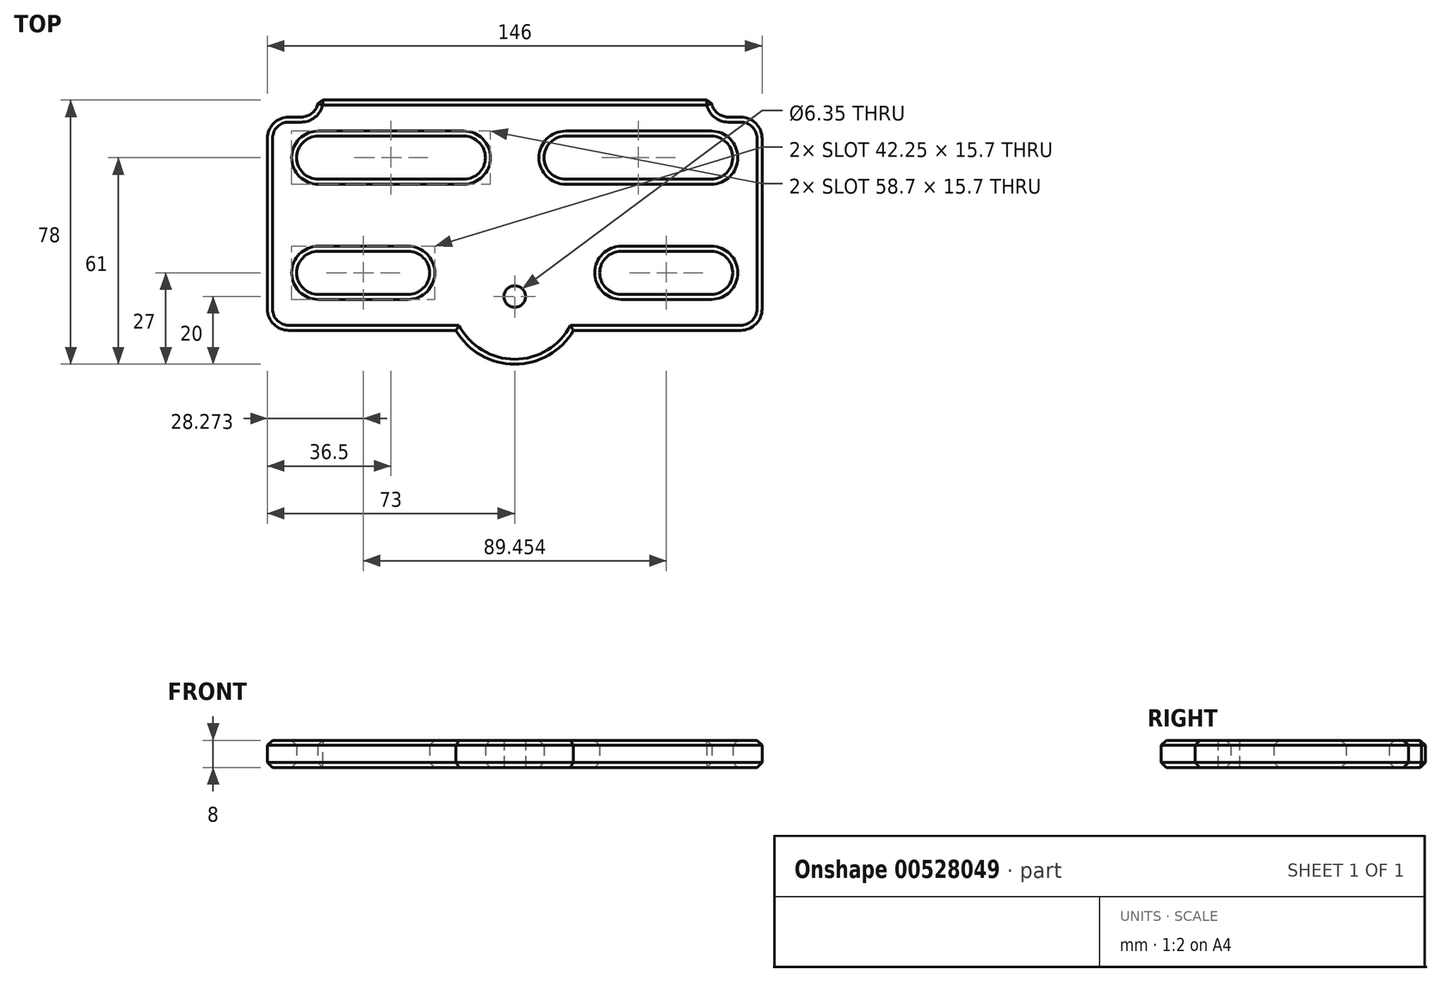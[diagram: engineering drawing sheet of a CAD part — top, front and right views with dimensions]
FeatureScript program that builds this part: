
annotation { "Feature Type Name" : "Feature", "Feature Type Description" : "" }
export const myFeature = defineFeature(function(context is Context, id is Id, definition is map)
    precondition{}
    {
        {
            var Q0;
            Q0=qCreatedBy(makeId("Top.planeOp"),FACE);
            var sketch = newSketch(context, id + "F0", { "sketchPlane" : qUnion([Q0])});
            skLineSegment(sketch, "E0", {"start": v(-66.65, -34) * mm, "end": v(-17.32, -34) * mm});
            skLineSegment(sketch, "E1", {"start": v(73, -27.65) * mm, "end": v(73, 22.65) * mm});
            skLineSegment(sketch, "E2", {"start": v(58, 34) * mm, "end": v(-58, 34) * mm});
            skLineSegment(sketch, "E3", {"start": v(-73, 22.65) * mm, "end": v(-73, -27.65) * mm});
            skArc(sketch, "E4", {"start": v(-17.32, -34) * mm, "mid": v(0, -44) * mm, "end": v(17.32, -34) * mm});
            skLineSegment(sketch, "E5.top", {"start": v(-66.65, 29) * mm, "end": v(-63, 29) * mm});
            skLineSegment(sketch, "E5.right", {"start": v(-58, 34) * mm, "end": v(-58, 34) * mm});
            skPoint(sketch, "E6.visualSharp", {"position": v(-58, 29) * mm});
            skArc(sketch, "E6.filletArc", {"start": v(-63, 29) * mm, "mid": v(-59.46, 30.46) * mm, "end": v(-58, 34) * mm});
            skLineSegment(sketch, "E7.top", {"start": v(66.65, 29) * mm, "end": v(63, 29) * mm});
            skLineSegment(sketch, "E7.right", {"start": v(58, 34) * mm, "end": v(58, 34) * mm});
            skPoint(sketch, "E8.visualSharp", {"position": v(58, 29) * mm});
            skArc(sketch, "E8.filletArc", {"start": v(58, 34) * mm, "mid": v(59.46, 30.46) * mm, "end": v(63, 29) * mm});
            skLineSegment(sketch, "E9.trimOffspring", {"start": v(17.32, -34) * mm, "end": v(66.65, -34) * mm});
            skPoint(sketch, "E10.visualSharp", {"position": v(-73, 29) * mm});
            skArc(sketch, "E10.filletArc", {"start": v(-66.65, 29) * mm, "mid": v(-71.14, 27.14) * mm, "end": v(-73, 22.65) * mm});
            skPoint(sketch, "E11.visualSharp", {"position": v(-73, -34) * mm});
            skArc(sketch, "E11.filletArc", {"start": v(-73, -27.65) * mm, "mid": v(-71.14, -32.14) * mm, "end": v(-66.65, -34) * mm});
            skPoint(sketch, "E12.visualSharp", {"position": v(73, -34) * mm});
            skArc(sketch, "E12.filletArc", {"start": v(66.65, -34) * mm, "mid": v(71.14, -32.14) * mm, "end": v(73, -27.65) * mm});
            skPoint(sketch, "E13.visualSharp", {"position": v(73, 29) * mm});
            skArc(sketch, "E13.filletArc", {"start": v(73, 22.65) * mm, "mid": v(71.14, 27.14) * mm, "end": v(66.65, 29) * mm});
            skLineSegment(sketch, "E14", {"start": v(-58, 17) * mm, "end": v(-15, 17) * mm});
            skLineSegment(sketch, "E15.MirrorCS", {"start": v(58, 17) * mm, "end": v(15, 17) * mm});
            skArc(sketch, "E16.0.startCap", {"start": v(-58, 10.65) * mm, "mid": v(-64.35, 17) * mm, "end": v(-58, 23.35) * mm});
            skArc(sketch, "E16.0.endCap", {"start": v(-15, 23.35) * mm, "mid": v(-8.65, 17) * mm, "end": v(-15, 10.65) * mm});
            skLineSegment(sketch, "E16.0.left", {"start": v(-58, 23.35) * mm, "end": v(-15, 23.35) * mm});
            skLineSegment(sketch, "E16.0.right", {"start": v(-58, 10.65) * mm, "end": v(-15, 10.65) * mm});
            skArc(sketch, "E17.0.startCap", {"start": v(58, 23.35) * mm, "mid": v(64.35, 17) * mm, "end": v(58, 10.65) * mm});
            skArc(sketch, "E17.0.endCap", {"start": v(15, 10.65) * mm, "mid": v(8.65, 17) * mm, "end": v(15, 23.35) * mm});
            skLineSegment(sketch, "E17.0.left", {"start": v(58, 10.65) * mm, "end": v(15, 10.65) * mm});
            skLineSegment(sketch, "E17.0.right", {"start": v(58, 23.35) * mm, "end": v(15, 23.35) * mm});
            skLineSegment(sketch, "E18", {"start": v(31.45, -17) * mm, "end": v(58, -17) * mm});
            skLineSegment(sketch, "E19.MirrorCS", {"start": v(-31.45, -17) * mm, "end": v(-58, -17) * mm});
            skArc(sketch, "E20.0.startCap", {"start": v(31.45, -23.35) * mm, "mid": v(25.1, -17) * mm, "end": v(31.45, -10.65) * mm});
            skArc(sketch, "E20.0.endCap", {"start": v(58, -10.65) * mm, "mid": v(64.35, -17) * mm, "end": v(58, -23.35) * mm});
            skLineSegment(sketch, "E20.0.left", {"start": v(31.45, -10.65) * mm, "end": v(58, -10.65) * mm});
            skLineSegment(sketch, "E20.0.right", {"start": v(31.45, -23.35) * mm, "end": v(58, -23.35) * mm});
            skArc(sketch, "E21.0.startCap", {"start": v(-31.45, -10.65) * mm, "mid": v(-25.1, -17) * mm, "end": v(-31.45, -23.35) * mm});
            skArc(sketch, "E21.0.endCap", {"start": v(-58, -23.35) * mm, "mid": v(-64.35, -17) * mm, "end": v(-58, -10.65) * mm});
            skLineSegment(sketch, "E21.0.left", {"start": v(-31.45, -23.35) * mm, "end": v(-58, -23.35) * mm});
            skLineSegment(sketch, "E21.0.right", {"start": v(-31.45, -10.65) * mm, "end": v(-58, -10.65) * mm});
            skCircle(sketch, "E22", {"center": v(0, -24) * mm, "radius": 3.18 * mm});
            skSolve(sketch);
        }
        {
            var Q0;
            Q0=makeQuery(id+"F0.imprint","IMPRINT",FACE,{"disambiguationData":[TD([[makeQuery(id+"F0.imprint","IMPRINT",EDGE,{"derivedFrom":sQuery(id+"F0.wireOp",EDGE,"E0")}),1.0]])]});
            extrude(context, id + "F1", {"entities" : qUnion([Q0]), "depth" : 8 * mm, "offsetDistance" : 25.4 * mm});
        }
        {
            var Q0;
            Q0=makeQuery(id+"F1.opExtrude","CAP_EDGE",EDGE,{"disambiguationData":[OSD([sQuery(id+"F0.wireOp",EDGE,"E2")])],"isStart":false});
            var Q1;
            Q1=makeQuery(id+"F1.opExtrude","CAP_EDGE",EDGE,{"disambiguationData":[OSD([sQuery(id+"F0.wireOp",EDGE,"E9.trimOffspring")])],"isStart":false});
            var Q2;
            Q2=makeQuery(id+"F1.opExtrude","CAP_EDGE",EDGE,{"disambiguationData":[OSD([sQuery(id+"F0.wireOp",EDGE,"E0")])],"isStart":false});
            var Q3;
            Q3=makeQuery(id+"F1.opExtrude","CAP_EDGE",EDGE,{"disambiguationData":[OSD([sQuery(id+"F0.wireOp",EDGE,"E4")])],"isStart":false});
            var Q4;
            Q4=makeQuery(id+"F1.opExtrude","CAP_EDGE",EDGE,{"disambiguationData":[OSD([sQuery(id+"F0.wireOp",EDGE,"E21.0.left")])],"isStart":false});
            var Q5;
            Q5=makeQuery(id+"F1.opExtrude","CAP_EDGE",EDGE,{"disambiguationData":[OSD([sQuery(id+"F0.wireOp",EDGE,"E16.0.right")])],"isStart":false});
            var Q6;
            Q6=makeQuery(id+"F1.opExtrude","CAP_EDGE",EDGE,{"disambiguationData":[OSD([sQuery(id+"F0.wireOp",EDGE,"E17.0.left")])],"isStart":false});
            var Q7;
            Q7=makeQuery(id+"F1.opExtrude","CAP_EDGE",EDGE,{"disambiguationData":[OSD([sQuery(id+"F0.wireOp",EDGE,"E20.0.right")])],"isStart":false});
            var Q8;
            Q8=makeQuery(id+"F1.opExtrude","SWEPT_EDGE",EDGE,{"disambiguationData":[OSD([sQuery(id+"F0.wireOp",EDGE,"E2"),sQuery(id+"F0.wireOp",EDGE,"E8.filletArc")])]});
            var Q9;
            Q9=makeQuery(id+"F1.opExtrude","SWEPT_EDGE",EDGE,{"disambiguationData":[OSD([sQuery(id+"F0.wireOp",EDGE,"E2"),sQuery(id+"F0.wireOp",EDGE,"E6.filletArc")])]});
            var Q10;
            Q10=makeQuery(id+"F1.opExtrude","CAP_EDGE",EDGE,{"disambiguationData":[OSD([sQuery(id+"F0.wireOp",EDGE,"E2")])],"isStart":true});
            var Q11;
            Q11=makeQuery(id+"F1.opExtrude","CAP_EDGE",EDGE,{"disambiguationData":[OSD([sQuery(id+"F0.wireOp",EDGE,"E1")])],"isStart":true});
            var Q12;
            Q12=makeQuery(id+"F1.opExtrude","CAP_EDGE",EDGE,{"disambiguationData":[OSD([sQuery(id+"F0.wireOp",EDGE,"E3")])],"isStart":true});
            var Q13;
            Q13=makeQuery(id+"F1.opExtrude","CAP_EDGE",EDGE,{"disambiguationData":[OSD([sQuery(id+"F0.wireOp",EDGE,"E4")])],"isStart":true});
            var Q14;
            Q14=makeQuery(id+"F1.opExtrude","CAP_EDGE",EDGE,{"disambiguationData":[OSD([sQuery(id+"F0.wireOp",EDGE,"E21.0.left")])],"isStart":true});
            var Q15;
            Q15=makeQuery(id+"F1.opExtrude","CAP_EDGE",EDGE,{"disambiguationData":[OSD([sQuery(id+"F0.wireOp",EDGE,"E16.0.right")])],"isStart":true});
            var Q16;
            Q16=makeQuery(id+"F1.opExtrude","CAP_EDGE",EDGE,{"disambiguationData":[OSD([sQuery(id+"F0.wireOp",EDGE,"E17.0.left")])],"isStart":true});
            var Q17;
            Q17=makeQuery(id+"F1.opExtrude","CAP_EDGE",EDGE,{"disambiguationData":[OSD([sQuery(id+"F0.wireOp",EDGE,"E20.0.left")])],"isStart":true});
            chamfer(context, id + "F2", {"entities" : qUnion([Q0, Q1, Q2, Q3, Q4, Q5, Q6, Q7, Q8, Q9, Q10, Q11, Q12, Q13, Q14, Q15, Q16, Q17]), "width" : 1.5 * mm, "tangentPropagation" : true});
        }
    });
